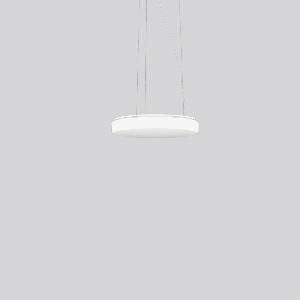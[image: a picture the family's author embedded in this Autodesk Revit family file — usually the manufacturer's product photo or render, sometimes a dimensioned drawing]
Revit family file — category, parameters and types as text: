
# Revit family: flat_polymero_kreis_slim_312089_002_4_76_ed09
name_source: partatom
category: Lighting Fixtures
units: mm (PartAtom-declared; Revit-internal decimal feet)

## family parameters
Cut with Voids When Loaded = No
Host = Face
Light Source = No
Part Type = Normal
Room Calculation Point = No
Round Connector Dimension = Use Diameter
Shared = No

## types (1)
- FLAT POLYMERO KREIS SLIM (1 x LED Modul 840, 2150 lm, 4000)
    Apparent Load = 19 VA
    CIE Flux Codes = 43 74 93 89 100
    Color Rendering = 80
    Color Temperature = 4000
    Default Elevation = 1800 mm
    Description = Series: FLAT POLYMERO KREIS SLIM
Decorative round LED pendant luminaire. Base and canopy: metal, powder-coated, white. Canopy Ø 205 mm, h 35 mm. Diffuser made of plastic (polycarbonate), opal, shockproof. Diffuser fastening: patented push system. Homogeneous and smooth light distribution. Suitable for pendant. 3-point steel cable suspension, steplessly adjustable. Special lengths available on request. TouchDim sensor capable. Light and/or presence sensors can be integrated. 
Colour: white
Diameter: 360 mm
Height: 61 mm
Suspension length: 200-1300 mm
Lamp: LED
Socket: without socket
Colour temperature: 4000K
Colour rendering index (CRI): 80
System power: 19 W
Rated luminous flux: 2150 lm
Luminous efficiency: 113 lm/W
Control gear: AC power, DALI dimmable
Protection class: I
Type of protection: IP 40
    Height = 61 mm
    Lamp = 1 x LED Modul 840
    Lamp Light Flux = 2150 lm
    Lamp count = 1
    Length = 360 mm
    Lifetime = 50000 h
    Luminous efficacy = 113 lm/W
    Manufacturer = RZB
    ModVariant = No
    Model = 312089.002.4.76
    Mounting Place = Ceiling
    Mounting Type = Pendant
    Number of Poles = 1
    OnlyDefault = Yes
    Power Factor = 1
    Product Name = FLAT POLYMERO KREIS SLIM
    Product group = Pendant luminaires
    ProductGroupID = 902
    Protection Class = Protection class I
    Protection Degree = IP 40
    RLX_Detail_Level = 1
    RLX_Emergency_Light_Flux = 0 lm
    RLX_Emergency_Type = 0
    RLX_Emergency_Type_DB = No
    RlxData = <blob elided: 57045 chars, md5=933d262a>
    Socket = socket
    Standby Power = 0 W
    System Light Flux = 2150 lm
    System Power = 19 W
    Type Comments = Product without accessories
    Type Image = 312089.002.jpg
    URL = http://relux.com
    VarID = ---
    Voltage = 230 V
    Voltage Range = 220-240 V
    Weight = 0.00 kg
    Width = 0 mm  [stored 0 ft]

note: [stored X ft] marks values corroborated as IEEE doubles in the binary element streams (Revit-internal decimal feet)

## geometry (parser evidence)
native form markers: Blend x4, Sweep x14
no freeform markers — native parametric forms only
